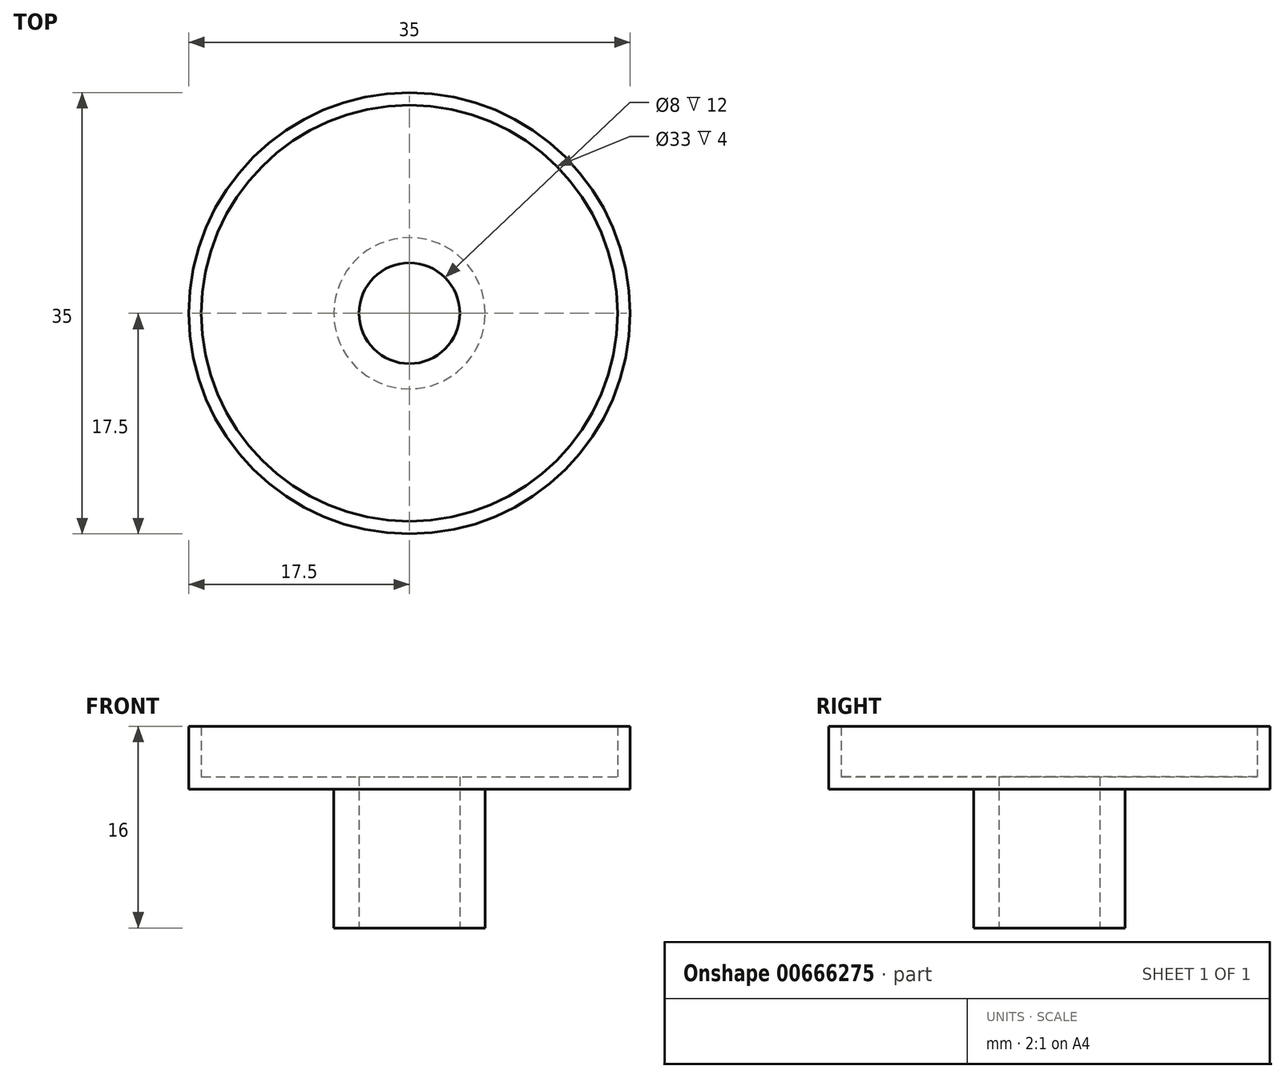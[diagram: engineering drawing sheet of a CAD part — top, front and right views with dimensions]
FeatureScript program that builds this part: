
annotation { "Feature Type Name" : "Feature", "Feature Type Description" : "" }
export const myFeature = defineFeature(function(context is Context, id is Id, definition is map)
    precondition{}
    {
        {
            var Q0;
            Q0=qCreatedBy(makeId("Front.planeOp"),FACE);
            var sketch = newSketch(context, id + "F0", { "sketchPlane" : qUnion([Q0])});
            skLineSegment(sketch, "E0", {"start": v(0, 0) * mm, "end": v(0, 16.7) * mm, "construction": true});
            skLineSegment(sketch, "E1", {"start": v(-4, 0) * mm, "end": v(-4, 12) * mm});
            skLineSegment(sketch, "E2", {"start": v(-4, 12) * mm, "end": v(-16.5, 12) * mm});
            skLineSegment(sketch, "E3", {"start": v(-16.5, 12) * mm, "end": v(-16.5, 39) * mm, "construction": true});
            skLineSegment(sketch, "E4", {"start": v(-16.5, 39) * mm, "end": v(0, 39) * mm, "construction": true});
            skLineSegment(sketch, "E5", {"start": v(0, 39) * mm, "end": v(0, 40) * mm, "construction": true});
            skLineSegment(sketch, "E6", {"start": v(0, 40) * mm, "end": v(-17.5, 40) * mm, "construction": true});
            skLineSegment(sketch, "E7", {"start": v(-17.5, 40) * mm, "end": v(-17.5, 11) * mm, "construction": true});
            skLineSegment(sketch, "E8", {"start": v(-17.5, 11) * mm, "end": v(-6, 11) * mm});
            skLineSegment(sketch, "E9", {"start": v(-6, 11) * mm, "end": v(-6, 0) * mm});
            skLineSegment(sketch, "E10", {"start": v(-6, 0) * mm, "end": v(-4, 0) * mm});
            skPoint(sketch, "E11", {"position": v(0, 39.5) * mm});
            skLineSegment(sketch, "E12", {"start": v(-17.5, 11) * mm, "end": v(-17.5, 16) * mm});
            skLineSegment(sketch, "E13", {"start": v(-17.5, 16) * mm, "end": v(-16.5, 16) * mm});
            skLineSegment(sketch, "E14", {"start": v(-16.5, 16) * mm, "end": v(-16.5, 12) * mm});
            skSolve(sketch);
        }
        {
            var Q0;
            Q0=qSketchRegion(id+"F0",true);
            var Q1;
            Q1=sQuery(id+"F0.wireOp",EDGE,"E0");
            revolve(context, id + "F1", {"surfaceOperationType" : NewSurfaceOperationType.NEW, "entities" : qUnion([Q0]), "axis" : qUnion([Q1]), "revolveType" : RevolveType.FULL});
        }
    });
